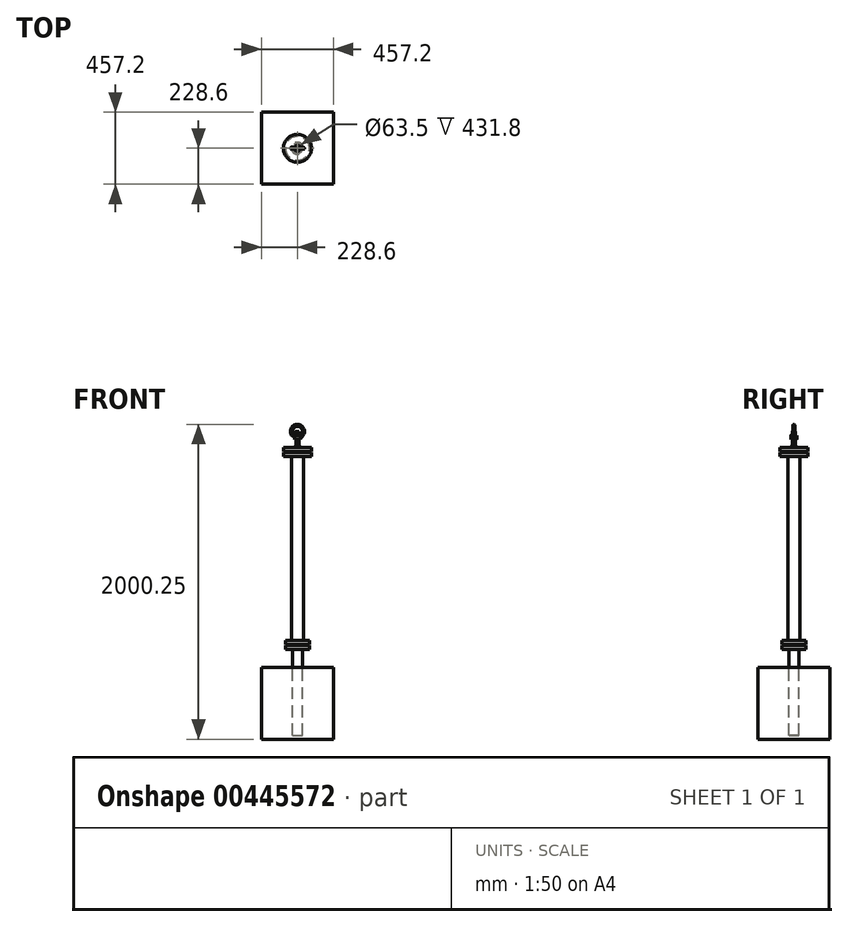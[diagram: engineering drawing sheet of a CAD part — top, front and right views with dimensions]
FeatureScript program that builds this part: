
annotation { "Feature Type Name" : "Feature", "Feature Type Description" : "" }
export const myFeature = defineFeature(function(context is Context, id is Id, definition is map)
    precondition{}
    {
        {
            var Q0;
            Q0=qCreatedBy(makeId("Top.planeOp"),FACE);
            var sketch = newSketch(context, id + "F0", { "sketchPlane" : qUnion([Q0])});
            skCircle(sketch, "E0", {"center": v(0, 0) * mm, "radius": 88.9 * mm});
            skSolve(sketch);
        }
        {
            var Q0;
            Q0=makeQuery(id+"F0.imprint","IMPRINT",FACE,{"disambiguationData":[TD([[makeQuery(id+"F0.imprint","IMPRINT",EDGE,{"derivedFrom":sQuery(id+"F0.wireOp",EDGE,"E0")}),1.0]])]});
            extrude(context, id + "F1", {"entities" : qUnion([Q0]), "oppositeDirection" : true, "depth" : 25.4 * mm});
        }
        {
            var Q0;
            Q0=makeQuery(id+"F1.opExtrude","CAP_FACE",FACE,{"disambiguationData":[OSD([sQuery(id+"F0.wireOp",EDGE,"E0")])],"isStart":true});
            var sketch = newSketch(context, id + "F2", { "sketchPlane" : qUnion([Q0])});
            skCircle(sketch, "E1", {"center": v(0, 0) * mm, "radius": 12.7 * mm});
            skSolve(sketch);
        }
        {
            var Q0;
            Q0=makeQuery(id+"F2.imprint","IMPRINT",FACE,{"disambiguationData":[TD([[makeQuery(id+"F2.imprint","IMPRINT",EDGE,{"derivedFrom":sQuery(id+"F2.wireOp",EDGE,"E1")}),1.0]])]});
            extrude(context, id + "F3", {"entities" : qUnion([Q0]), "operationType" : NewBodyOperationType.ADD, "depth" : 12.7 * mm});
        }
        {
            var Q0;
            Q0=makeQuery(id+"F3.opExtrude","CAP_FACE",FACE,{"disambiguationData":[OSD([sQuery(id+"F2.wireOp",EDGE,"E1")])],"isStart":false});
            var sketch = newSketch(context, id + "F4", { "sketchPlane" : qUnion([Q0])});
            skCircle(sketch, "E2.0.0", {"center": v(0, 0) * mm, "radius": 12.7 * mm});
            skCircle(sketch, "E3", {"center": v(0, 0) * mm, "radius": 9.53 * mm});
            skSolve(sketch);
        }
        {
            var Q0;
            Q0=makeQuery(id+"F4.imprint","IMPRINT",FACE,{"disambiguationData":[TD([[makeQuery(id+"F4.imprint","IMPRINT",EDGE,{"derivedFrom":sQuery(id+"F4.wireOp",EDGE,"E3")}),1.0]])]});
            extrude(context, id + "F5", {"entities" : qUnion([Q0]), "operationType" : NewBodyOperationType.ADD, "depth" : 88.9 * mm});
        }
        {
            var Q0;
            Q0=makeQuery(id+"F5.opExtrude","CAP_FACE",FACE,{"disambiguationData":[OSD([sQuery(id+"F4.wireOp",EDGE,"E3")])],"isStart":false});
            var sketch = newSketch(context, id + "F6", { "sketchPlane" : qUnion([Q0])});
            skCircle(sketch, "E4.0.0", {"center": v(0, 0) * mm, "radius": 9.53 * mm});
            skSolve(sketch);
        }
        {
            var Q0;
            Q0=qCreatedBy(makeId("Front.planeOp"),FACE);
            var sketch = newSketch(context, id + "F7", { "sketchPlane" : qUnion([Q0])});
            skPoint(sketch, "E5.0", {"position": v(0, 101.6) * mm});
            skCircle(sketch, "E6", {"center": v(0, 101.6) * mm, "radius": 38.1 * mm});
            skSolve(sketch);
        }
        {
            var Q0;
            Q0=qCreatedBy(makeId("Right.planeOp"),FACE);
            var sketch = newSketch(context, id + "F8", { "sketchPlane" : qUnion([Q0])});
            skLineSegment(sketch, "E7.0", {"start": v(0, 63.5) * mm, "end": v(0, 139.7) * mm});
            skCircle(sketch, "E8", {"center": v(0, 139.7) * mm, "radius": 6.35 * mm});
            skSolve(sketch);
        }
        {
            var Q0;
            Q0=makeQuery(id+"F8.imprint","IMPRINT",FACE,{"disambiguationData":[TD([[makeQuery(id+"F8.imprint","IMPRINT",EDGE,{"derivedFrom":sQuery(id+"F8.wireOp",EDGE,"E8")}),1.0]])]});
            var Q1;
            Q1=sQuery(id+"F7.wireOp",EDGE,"E6");
            sweep(context, id + "F9", {"operationType" : NewBodyOperationType.ADD, "profiles" : qUnion([Q0]), "path" : qUnion([Q1])});
        }
        {
            var Q0;
            Q0=qCreatedBy(makeId("Top.planeOp"),FACE);
            cPlane(context, id + "F10", {"entities" : qUnion([Q0]), "cplaneType" : CPlaneType.OFFSET, "offset" : 76.2 * mm, "width" : 152.4 * mm, "height" : 152.4 * mm});
        }
        {
            var Q0;
            Q0=qCreatedBy(id+"F10.planeOp",FACE);
            var sketch = newSketch(context, id + "F11", { "sketchPlane" : qUnion([Q0])});
            skPoint(sketch, "E9.0", {"position": v(0, 0) * mm});
            skCircle(sketch, "E10", {"center": v(0, 0) * mm, "radius": 19.05 * mm});
            skSolve(sketch);
        }
        {
            var Q0;
            Q0=makeQuery(id+"F11.imprint","IMPRINT",FACE,{"disambiguationData":[TD([[makeQuery(id+"F11.imprint","IMPRINT",EDGE,{"derivedFrom":sQuery(id+"F11.wireOp",EDGE,"E10")}),1.0]])]});
            var Q1;
            Q1=sQuery(id+"F11.wireOp",EDGE,"E10");
            extrude(context, id + "F12", {"entities" : qUnion([Q0]), "surfaceEntities" : qUnion([Q1]), "oppositeDirection" : true, "depth" : 25.4 * mm});
        }
        {
            var Q0;
            Q0=makeQuery(id+"F1.opExtrude","CAP_FACE",FACE,{"disambiguationData":[OSD([sQuery(id+"F0.wireOp",EDGE,"E0")])],"isStart":false});
            cPlane(context, id + "F13", {"entities" : qUnion([Q0]), "cplaneType" : CPlaneType.OFFSET, "offset" : 6.35 * mm, "width" : 152.4 * mm, "height" : 152.4 * mm});
        }
        {
            var Q0;
            Q0=qCreatedBy(id+"F13.planeOp",FACE);
            var sketch = newSketch(context, id + "F14", { "sketchPlane" : qUnion([Q0])});
            skCircle(sketch, "E11.0.0", {"center": v(0, 0) * mm, "radius": 88.9 * mm});
            skSolve(sketch);
        }
        {
            var Q0;
            Q0=makeQuery(id+"F14.imprint","IMPRINT",FACE,{"disambiguationData":[TD([[makeQuery(id+"F14.imprint","IMPRINT",EDGE,{"derivedFrom":sQuery(id+"F14.wireOp",EDGE,"E11.0.0")}),1.0]])]});
            extrude(context, id + "F15", {"entities" : qUnion([Q0]), "depth" : 25.4 * mm});
        }
        {
            var Q0;
            Q0=makeQuery(id+"F15.opExtrude","CAP_FACE",FACE,{"disambiguationData":[OSD([sQuery(id+"F14.wireOp",EDGE,"E11.0.0")])],"isStart":false});
            var sketch = newSketch(context, id + "F16", { "sketchPlane" : qUnion([Q0])});
            skCircle(sketch, "E12.0.0", {"center": v(0, 0) * mm, "radius": 88.9 * mm});
            skCircle(sketch, "E13", {"center": v(0, 0) * mm, "radius": 38.1 * mm});
            skSolve(sketch);
        }
        {
            var Q0;
            Q0=makeQuery(id+"F16.imprint","IMPRINT",FACE,{"disambiguationData":[TD([[makeQuery(id+"F16.imprint","IMPRINT",EDGE,{"derivedFrom":sQuery(id+"F16.wireOp",EDGE,"E13")}),1.0]])]});
            extrude(context, id + "F17", {"entities" : qUnion([Q0]), "operationType" : NewBodyOperationType.ADD, "depth" : 1168.4 * mm});
        }
        {
            var Q0;
            Q0=makeQuery(id+"F17.opExtrude","CAP_FACE",FACE,{"disambiguationData":[OSD([sQuery(id+"F16.wireOp",EDGE,"E13")])],"isStart":false});
            var sketch = newSketch(context, id + "F18", { "sketchPlane" : qUnion([Q0])});
            skCircle(sketch, "E14.0.0", {"center": v(0, 0) * mm, "radius": 38.1 * mm});
            skCircle(sketch, "E15", {"center": v(0, 0) * mm, "radius": 76.2 * mm});
            skSolve(sketch);
        }
        {
            var Q0;
            Q0=makeQuery(id+"F18.imprint","IMPRINT",FACE,{"disambiguationData":[TD([[makeQuery(id+"F18.imprint","IMPRINT",EDGE,{"derivedFrom":sQuery(id+"F18.wireOp",EDGE,"E14.0.0")}),1.0]])]});
            var Q1;
            Q1=makeQuery(id+"F18.imprint","IMPRINT",FACE,{"disambiguationData":[TD([[makeQuery(id+"F18.imprint","IMPRINT",EDGE,{"derivedFrom":sQuery(id+"F18.wireOp",EDGE,"E14.0.0")}),-1.0]])]});
            extrude(context, id + "F19", {"entities" : qUnion([Q0, Q1]), "operationType" : NewBodyOperationType.ADD, "depth" : 25.4 * mm});
        }
        {
            var Q0;
            Q0=makeQuery(id+"F19.opExtrude","CAP_FACE",FACE,{"disambiguationData":[OSD([sQuery(id+"F18.wireOp",EDGE,"E15")])],"isStart":false});
            cPlane(context, id + "F20", {"entities" : qUnion([Q0]), "cplaneType" : CPlaneType.OFFSET, "offset" : 6.35 * mm, "width" : 152.4 * mm, "height" : 152.4 * mm});
        }
        {
            var Q0;
            Q0=qCreatedBy(id+"F20.planeOp",FACE);
            var sketch = newSketch(context, id + "F21", { "sketchPlane" : qUnion([Q0])});
            skCircle(sketch, "E16.0.0", {"center": v(0, 0) * mm, "radius": 76.2 * mm});
            skSolve(sketch);
        }
        {
            var Q0;
            Q0=makeQuery(id+"F21.imprint","IMPRINT",FACE,{"disambiguationData":[TD([[makeQuery(id+"F21.imprint","IMPRINT",EDGE,{"derivedFrom":sQuery(id+"F21.wireOp",EDGE,"E16.0.0")}),1.0]])]});
            extrude(context, id + "F22", {"entities" : qUnion([Q0]), "depth" : 25.4 * mm});
        }
        {
            var Q0;
            Q0=makeQuery(id+"F22.opExtrude","CAP_FACE",FACE,{"disambiguationData":[OSD([sQuery(id+"F21.wireOp",EDGE,"E16.0.0")])],"isStart":false});
            var sketch = newSketch(context, id + "F23", { "sketchPlane" : qUnion([Q0])});
            skCircle(sketch, "E17", {"center": v(0, 0) * mm, "radius": 31.75 * mm});
            skSolve(sketch);
        }
        {
            var Q0;
            Q0=makeQuery(id+"F23.imprint","IMPRINT",FACE,{"disambiguationData":[TD([[makeQuery(id+"F23.imprint","IMPRINT",EDGE,{"derivedFrom":sQuery(id+"F23.wireOp",EDGE,"E17")}),1.0]])]});
            extrude(context, id + "F24", {"entities" : qUnion([Q0]), "operationType" : NewBodyOperationType.ADD, "depth" : 114.3 * mm});
        }
        {
            var Q0;
            Q0=makeQuery(id+"F24.opExtrude","CAP_FACE",FACE,{"disambiguationData":[OSD([sQuery(id+"F23.wireOp",EDGE,"E17")])],"isStart":false});
            var sketch = newSketch(context, id + "F25", { "sketchPlane" : qUnion([Q0])});
            skLineSegment(sketch, "E18.bottom", {"start": v(228.6, -228.6) * mm, "end": v(-228.6, -228.6) * mm});
            skLineSegment(sketch, "E18.top", {"start": v(228.6, 228.6) * mm, "end": v(-228.6, 228.6) * mm});
            skLineSegment(sketch, "E18.left", {"start": v(228.6, -228.6) * mm, "end": v(228.6, 228.6) * mm});
            skLineSegment(sketch, "E18.right", {"start": v(-228.6, -228.6) * mm, "end": v(-228.6, 228.6) * mm});
            skPoint(sketch, "E18.middle", {"position": v(0, 0) * mm});
            skSolve(sketch);
        }
        {
            var Q0;
            Q0=makeQuery(id+"F25.imprint","IMPRINT",FACE,{"disambiguationData":[TD([[makeQuery(id+"F25.imprint","IMPRINT",EDGE,{"derivedFrom":sQuery(id+"F25.wireOp",EDGE,"E18.bottom")}),-1.0]])]});
            extrude(context, id + "F26", {"entities" : qUnion([Q0]), "operationType" : NewBodyOperationType.ADD, "depth" : 457.2 * mm});
        }
        {
            var Q0;
            Q0=makeQuery(id+"F26.opExtrude","CAP_FACE",FACE,{"disambiguationData":[OSD([sQuery(id+"F23.wireOp",EDGE,"E17"),sQuery(id+"F25.wireOp",EDGE,"E18.bottom"),sQuery(id+"F25.wireOp",EDGE,"E18.top"),sQuery(id+"F25.wireOp",EDGE,"E18.left"),sQuery(id+"F25.wireOp",EDGE,"E18.right")])],"isStart":false});
            var sketch = newSketch(context, id + "F27", { "sketchPlane" : qUnion([Q0])});
            skCircle(sketch, "E19.0", {"center": v(0, 0) * mm, "radius": 31.75 * mm});
            skSolve(sketch);
        }
        {
            var Q0;
            Q0=makeQuery(id+"F27.imprint","IMPRINT",FACE,{"disambiguationData":[TD([[makeQuery(id+"F27.imprint","IMPRINT",EDGE,{"derivedFrom":sQuery(id+"F27.wireOp",EDGE,"E19.0")}),1.0]])]});
            extrude(context, id + "F28", {"entities" : qUnion([Q0]), "operationType" : NewBodyOperationType.ADD, "oppositeDirection" : true, "depth" : 25.4 * mm});
        }
    });
